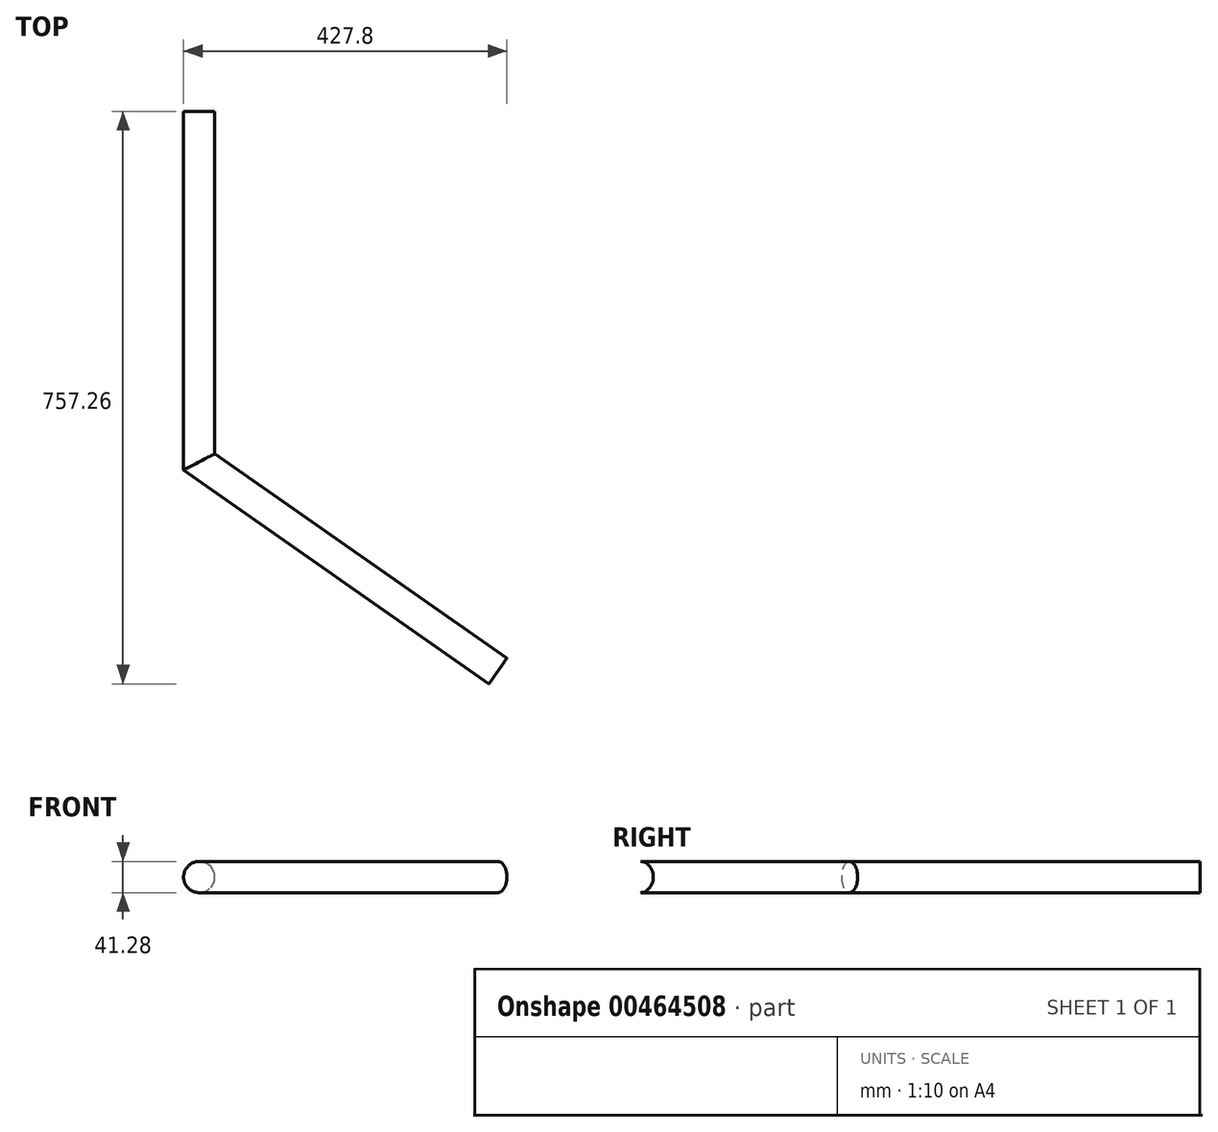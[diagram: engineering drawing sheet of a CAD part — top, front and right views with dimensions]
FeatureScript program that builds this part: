
annotation { "Feature Type Name" : "Feature", "Feature Type Description" : "" }
export const myFeature = defineFeature(function(context is Context, id is Id, definition is map)
    precondition{}
    {
        {
            var Q0;
            Q0=qCreatedBy(makeId("Top.planeOp"),FACE);
            var sketch = newSketch(context, id + "F0", { "sketchPlane" : qUnion([Q0])});
            skLineSegment(sketch, "E0", {"start": v(0, 0) * mm, "end": v(0, -463.55) * mm});
            skCircle(sketch, "E1", {"center": v(0, -463.55) * mm, "radius": 20.64 * mm});
            skLineSegment(sketch, "E2", {"start": v(0, -463.55) * mm, "end": v(395.32, -740.36) * mm});
            skLineSegment(sketch, "E3", {"start": v(0, -463.55) * mm, "end": v(-53.73, -540.28) * mm});
            skSolve(sketch);
        }
        {
            var Q0;
            Q0=qCreatedBy(makeId("Front.planeOp"),FACE);
            var sketch = newSketch(context, id + "F1", { "sketchPlane" : qUnion([Q0])});
            skCircle(sketch, "E4", {"center": v(0, 0) * mm, "radius": 20.64 * mm});
            skSolve(sketch);
        }
        {
            var Q0;
            Q0=makeQuery(id+"F1.imprint","IMPRINT",FACE,{"disambiguationData":[TD([[makeQuery(id+"F1.imprint","IMPRINT",EDGE,{"derivedFrom":sQuery(id+"F1.wireOp",EDGE,"E4")}),1.0]])]});
            var Q1;
            Q1=sQuery(id+"F0.wireOp",EDGE,"E0");
            var Q2;
            Q2=sQuery(id+"F0.wireOp",EDGE,"E2");
            sweep(context, id + "F2", {"profiles" : qUnion([Q0]), "path" : qUnion([Q1, Q2])});
        }
    });
